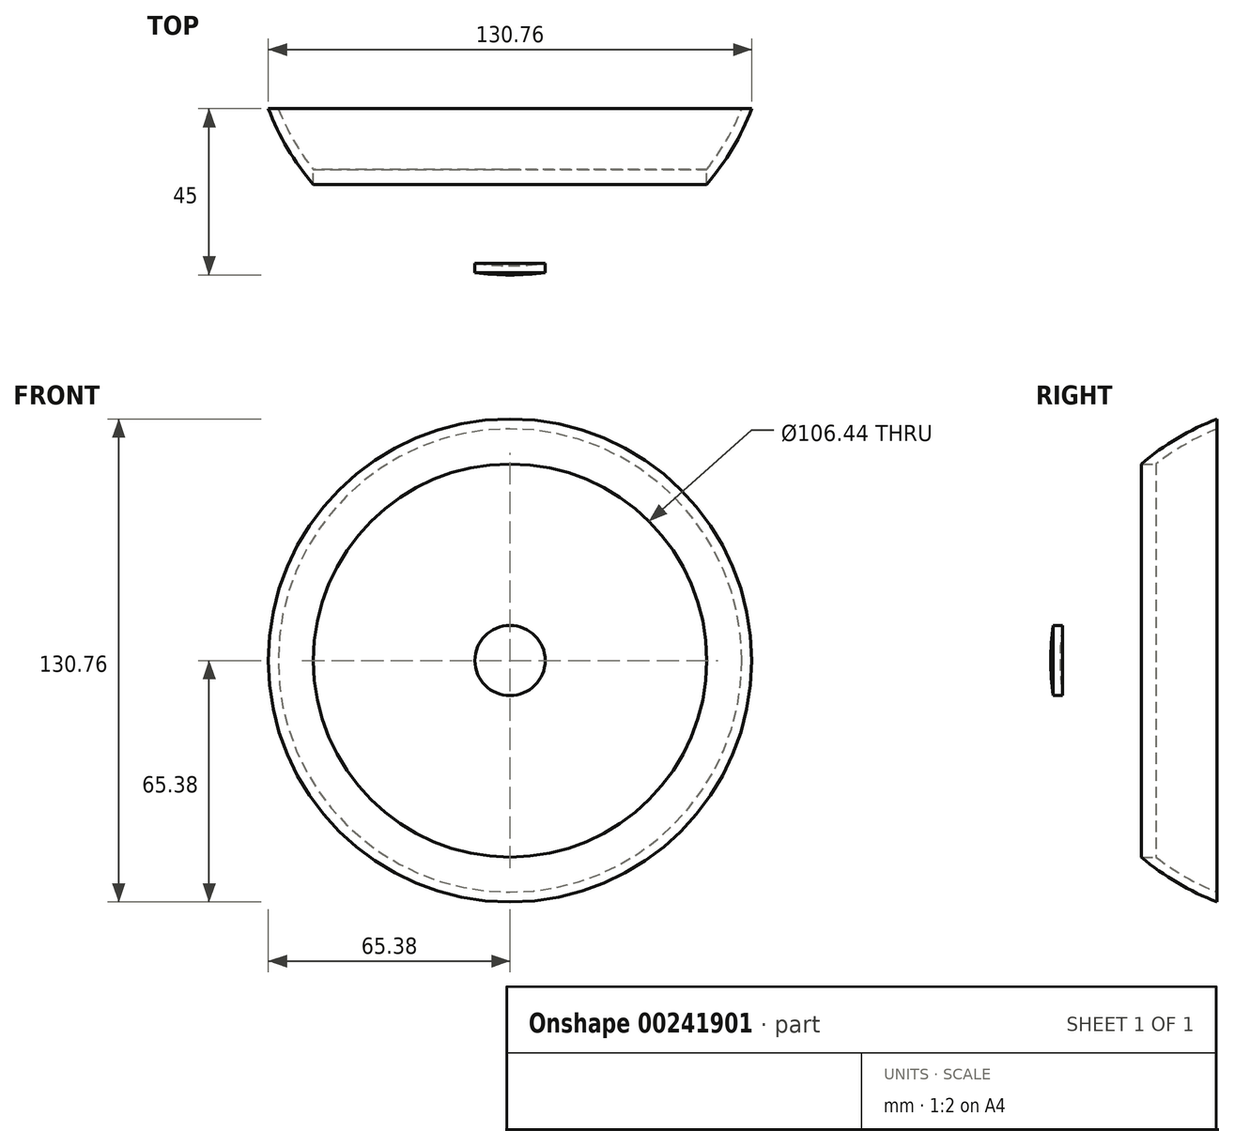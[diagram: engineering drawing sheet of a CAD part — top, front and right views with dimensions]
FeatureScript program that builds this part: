
annotation { "Feature Type Name" : "Feature", "Feature Type Description" : "" }
export const myFeature = defineFeature(function(context is Context, id is Id, definition is map)
    precondition{}
    {
        {
            var Q0;
            Q0=qCreatedBy(makeId("Front.planeOp"),FACE);
            var sketch = newSketch(context, id + "F0", { "sketchPlane" : qUnion([Q0])});
            skCircle(sketch, "E0", {"center": v(0, 0) * mm, "radius": 70 * mm});
            skCircle(sketch, "E1", {"center": v(0, 0) * mm, "radius": 67.5 * mm});
            skLineSegment(sketch, "E2", {"start": v(0, 70) * mm, "end": v(0, -70) * mm});
            skCircle(sketch, "E3", {"center": v(0, 0) * mm, "radius": 53.22 * mm});
            skCircle(sketch, "E4", {"center": v(0, 0) * mm, "radius": 9.5 * mm});
            skLineSegment(sketch, "E5", {"start": v(0, 0) * mm, "end": v(22.94, 48.02) * mm});
            skLineSegment(sketch, "E6", {"start": v(0, 0) * mm, "end": v(39.57, 35.6) * mm});
            skLineSegment(sketch, "E7", {"start": v(50.18, 17.74) * mm, "end": v(0, 0) * mm});
            skLineSegment(sketch, "E8", {"start": v(53.15, -2.81) * mm, "end": v(0, 0) * mm});
            skLineSegment(sketch, "E9", {"start": v(0, 0) * mm, "end": v(48.02, -22.94) * mm});
            skLineSegment(sketch, "E10", {"start": v(35.6, -39.57) * mm, "end": v(0, 0) * mm});
            skLineSegment(sketch, "E11", {"start": v(0, 0) * mm, "end": v(17.74, -50.18) * mm});
            skLineSegment(sketch, "E12", {"start": v(-2.72, -53.15) * mm, "end": v(0, 0) * mm});
            skLineSegment(sketch, "E13", {"start": v(0, 0) * mm, "end": v(-22.85, -48.06) * mm});
            skLineSegment(sketch, "E14", {"start": v(2.81, 53.15) * mm, "end": v(0, 0) * mm});
            skLineSegment(sketch, "E15", {"start": v(0, 0) * mm, "end": v(-17.74, 50.18) * mm});
            skLineSegment(sketch, "E16", {"start": v(0, 0) * mm, "end": v(-35.6, 39.57) * mm});
            skLineSegment(sketch, "E17", {"start": v(0, 0) * mm, "end": v(-48.02, 22.94) * mm});
            skLineSegment(sketch, "E18", {"start": v(0, 0) * mm, "end": v(-53.15, 2.72) * mm});
            skLineSegment(sketch, "E19", {"start": v(0, 0) * mm, "end": v(-50.15, -17.83) * mm});
            skLineSegment(sketch, "E20", {"start": v(0, 0) * mm, "end": v(-39.5, -35.66) * mm});
            skSolve(sketch);
        }
        {
            var Q0;
            {var subQ0=sQuery(id+"F0.wireOp",EDGE,"E2");var subQ1=sQuery(id+"F0.wireOp",EDGE,"E0");var subQ2=makeQuery(id+"F0.imprint","INTERSECT",VERTEX,{"disambiguationData":[OD(0.0)],"derivedFrom":[subQ1,subQ0]});Q0=makeQuery(id+"F0.imprint","IMPRINT",FACE,{"disambiguationData":[TD([[makeQuery(id+"F0.imprint","IMPRINT",EDGE,{"disambiguationData":[TD([[subQ2,-1.0]])],"derivedFrom":subQ1}),1.0]])]});}
            var Q1;
            Q1=sQuery(id+"F0.wireOp",EDGE,"E2");
            revolve(context, id + "F1", {"entities" : qUnion([Q0]), "axis" : qUnion([Q1]), "revolveType" : RevolveType.FULL});
        }
        {
            var Q0;
            Q0=qCreatedBy(makeId("Right.planeOp"),FACE);
            var sketch = newSketch(context, id + "F2", { "sketchPlane" : qUnion([Q0])});
            skLineSegment(sketch, "E21.bottom", {"start": v(-25, 71.68) * mm, "end": v(73.02, 71.68) * mm});
            skLineSegment(sketch, "E21.top", {"start": v(-25, -72.51) * mm, "end": v(73.02, -72.51) * mm});
            skLineSegment(sketch, "E21.left", {"start": v(-25, 71.68) * mm, "end": v(-25, -72.51) * mm});
            skLineSegment(sketch, "E21.right", {"start": v(73.02, 71.68) * mm, "end": v(73.02, -72.51) * mm});
            skSolve(sketch);
        }
        {
            var Q0;
            Q0=makeQuery(id+"F2.imprint","IMPRINT",FACE,{"disambiguationData":[TD([[makeQuery(id+"F2.imprint","IMPRINT",EDGE,{"derivedFrom":sQuery(id+"F2.wireOp",EDGE,"E21.bottom")}),-1.0]])]});
            extrude(context, id + "F3", {"entities" : qUnion([Q0]), "operationType" : NewBodyOperationType.REMOVE, "endBound" : BoundingType.THROUGH_ALL, "oppositeDirection" : true, "depth" : 25 * mm, "hasSecondDirection" : true, "secondDirectionBound" : SecondDirectionBoundingType.THROUGH_ALL, "secondDirectionOppositeDirection" : false, "secondDirectionDepth" : 25 * mm});
        }
        {
            var Q0;
            {var subQ0=sQuery(id+"F0.wireOp",EDGE,"E3");var subQ1=sQuery(id+"F0.wireOp",EDGE,"E2");var subQ2=makeQuery(id+"F0.imprint","INTERSECT",VERTEX,{"disambiguationData":[OD(0.0)],"derivedFrom":[subQ1,subQ0]});Q0=makeQuery(id+"F0.imprint","IMPRINT",FACE,{"disambiguationData":[TD([[makeQuery(id+"F0.imprint","IMPRINT",EDGE,{"disambiguationData":[TD([[subQ2,-1.0]])],"derivedFrom":subQ1}),-1.0]])]});}
            var Q1;
            {var subQ0=sQuery(id+"F0.wireOp",EDGE,"E5");var subQ1=sQuery(id+"F0.wireOp",EDGE,"E3");var subQ2=makeQuery(id+"F0.imprint","INTERSECT",VERTEX,{"derivedFrom":[subQ1,subQ0]});Q1=makeQuery(id+"F0.imprint","IMPRINT",FACE,{"disambiguationData":[TD([[makeQuery(id+"F0.imprint","IMPRINT",EDGE,{"disambiguationData":[TD([[subQ2,1.0]])],"derivedFrom":subQ1}),1.0]])]});}
            var Q2;
            {var subQ0=sQuery(id+"F0.wireOp",EDGE,"E7");var subQ1=sQuery(id+"F0.wireOp",EDGE,"E3");var subQ2=makeQuery(id+"F0.imprint","INTERSECT",VERTEX,{"derivedFrom":[subQ1,subQ0]});Q2=makeQuery(id+"F0.imprint","IMPRINT",FACE,{"disambiguationData":[TD([[makeQuery(id+"F0.imprint","IMPRINT",EDGE,{"disambiguationData":[TD([[subQ2,1.0]])],"derivedFrom":subQ1}),1.0]])]});}
            var Q3;
            {var subQ0=sQuery(id+"F0.wireOp",EDGE,"E9");var subQ1=sQuery(id+"F0.wireOp",EDGE,"E3");var subQ2=makeQuery(id+"F0.imprint","INTERSECT",VERTEX,{"derivedFrom":[subQ1,subQ0]});Q3=makeQuery(id+"F0.imprint","IMPRINT",FACE,{"disambiguationData":[TD([[makeQuery(id+"F0.imprint","IMPRINT",EDGE,{"disambiguationData":[TD([[subQ2,1.0]])],"derivedFrom":subQ1}),1.0]])]});}
            var Q4;
            {var subQ0=sQuery(id+"F0.wireOp",EDGE,"E4");var subQ1=sQuery(id+"F0.wireOp",EDGE,"E2");var subQ2=makeQuery(id+"F0.imprint","INTERSECT",VERTEX,{"disambiguationData":[OD(1.0)],"derivedFrom":[subQ1,subQ0]});Q4=makeQuery(id+"F0.imprint","IMPRINT",FACE,{"disambiguationData":[TD([[makeQuery(id+"F0.imprint","IMPRINT",EDGE,{"disambiguationData":[TD([[subQ2,-1.0]])],"derivedFrom":subQ1}),1.0]])]});}
            var Q5;
            {var subQ0=sQuery(id+"F0.wireOp",EDGE,"E13");var subQ1=sQuery(id+"F0.wireOp",EDGE,"E3");var subQ2=makeQuery(id+"F0.imprint","INTERSECT",VERTEX,{"derivedFrom":[subQ1,subQ0]});Q5=makeQuery(id+"F0.imprint","IMPRINT",FACE,{"disambiguationData":[TD([[makeQuery(id+"F0.imprint","IMPRINT",EDGE,{"disambiguationData":[TD([[subQ2,1.0]])],"derivedFrom":subQ1}),1.0]])]});}
            var Q6;
            {var subQ0=sQuery(id+"F0.wireOp",EDGE,"E18");var subQ1=sQuery(id+"F0.wireOp",EDGE,"E3");var subQ2=makeQuery(id+"F0.imprint","INTERSECT",VERTEX,{"derivedFrom":[subQ1,subQ0]});Q6=makeQuery(id+"F0.imprint","IMPRINT",FACE,{"disambiguationData":[TD([[makeQuery(id+"F0.imprint","IMPRINT",EDGE,{"disambiguationData":[TD([[subQ2,-1.0]])],"derivedFrom":subQ1}),1.0]])]});}
            var Q7;
            {var subQ0=sQuery(id+"F0.wireOp",EDGE,"E16");var subQ1=sQuery(id+"F0.wireOp",EDGE,"E3");var subQ2=makeQuery(id+"F0.imprint","INTERSECT",VERTEX,{"derivedFrom":[subQ1,subQ0]});Q7=makeQuery(id+"F0.imprint","IMPRINT",FACE,{"disambiguationData":[TD([[makeQuery(id+"F0.imprint","IMPRINT",EDGE,{"disambiguationData":[TD([[subQ2,-1.0]])],"derivedFrom":subQ1}),1.0]])]});}
            extrude(context, id + "F4", {"entities" : qUnion([Q0, Q1, Q2, Q3, Q4, Q5, Q6, Q7]), "operationType" : NewBodyOperationType.REMOVE, "endBound" : BoundingType.THROUGH_ALL, "depth" : 25 * mm});
        }
    });
